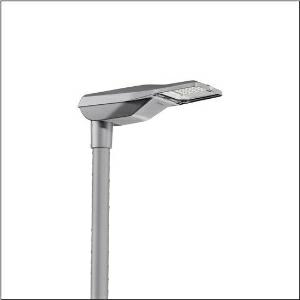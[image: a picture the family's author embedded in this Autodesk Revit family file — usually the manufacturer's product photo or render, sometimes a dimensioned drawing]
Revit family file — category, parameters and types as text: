
# Revit family: streetlight_sl_21_iq_micro___p0_5a_5xe1v31g08db_d973
name_source: partatom
category: Lighting Fixtures
units: mm (PartAtom-declared; Revit-internal decimal feet)

## family parameters
Cut with Voids When Loaded = No
Host = Face
Light Source = No
Part Type = Normal
Room Calculation Point = No
Round Connector Dimension = Use Diameter
Shared = No

## types (1)
- --- (1 x LED, 4660 lm, 36.4 W, 3000K)
    Apparent Load = 36 VA
    CIE Flux Codes = 37 73 96 100 100
    Color Rendering = 70
    Color Temperature = 3000K
    Default Elevation = 1800 mm
    Description = Streetlight SL 21 iQ micro, mast luminaire, primary light control with lens, of PMMA, primary optical cover: cover, of toughened safety glass, transparent, light distribution: P0.5a, light emission: direct distribution, primary light characteristic: asymmetric, installation type: post-top, side-entry, LED, High Power LED, rated luminous flux: 4.660lm, luminous efficacy: 128lm/W, light colour: 730, colour temperature: 3000K, control gear: iQ Street-Remote, control: pre-setting: linear dimming characteristic, Street-Remote, Auto-Match, Temp-Guard, Lumen-Switch, Night-Set, Smart-Wire, Light-Fading, Desk-Remote (wireless, voltage-free reading and setting of iQ features in the workshop via application-optimized NFC function/RFID function), optimised constant luminous flux control (CLO 2.0), mains connection: 220..240V, AC, 50/60Hz, start of lifetime: 36W, end of service life: 38W, reduction: 16W, luminaire housing, of diecast aluminium, powder-coated, Siteco® metallic grey (DB 702S), corrosivity category C5 mid according to DIN EN ISO 12944, please order mast flange separately, inclination adjustable: 0°, 5°, 10°, 15°, sealing non-destructively replaceable, multi-level sealing system, length: 528mm, width: 235mm, height: 110mm, mast flange for spigot size: 42mm (side-entry): 5XC10008XM4, 60/48mm (side-entry/post-top): 5XC10108XM2, 76/60mm (side-entry/post-top): 5XC10108XM1, protection rating (complete): IP66, insulation class (complete): insulation class II (safety insulation), certification: CE, ENEC, ENEC+, VDE, impact resistance: IK10, permissible operating ambient temperature for outdoor applications: -40..+50°C, standard-compliant lighting for roads and squares, packaging unit: 1 piece

Light Distribution: P0.5a
    Height = 110 mm
    Lamp = 1 x LED
    Lamp Light Flux = 4660 lm
    Lamp Power = 36.4 W
    Lamp count = 1
    Length = 528 mm
    Luminous efficacy = 128 lm/W
    Manufacturer = Siteco
    ModVariant = No
    Model = 5XE1V31G08DB
    Number of Poles = 1
    OnlyDefault = Yes
    Power Factor = 1
    Product Name = Streetlight SL 21 iQ micro | P0.5a
    Product group = mast luminaire | pylon top
    ProductGroupID = 6100
    Protection Class = Protection class II
    Protection Degree = IP 66
    RLX_Detail_Level = 1
    RLX_Emergency_Light_Flux = 0 lm
    RLX_Emergency_Type = 0
    RLX_Emergency_Type_DB = No
    RlxData = <blob elided: 98553 chars, md5=35e604e4>
    Socket = socket
    Standby Power = 0 W
    System Light Flux = 4660 lm
    System Power = 36 W
    Type Comments = factory setting: luminous flux: 100 % | dim-lin: 254 | 715 mA
    Type Image = l_1006881.jpg
    URL = http://relux.com
    VarID = @adj_070366
    Voltage = 0 V
    Weight = 0.00 kg
    Width = 235 mm

## geometry (parser evidence)
native form markers: Blend x4, Sweep x10
no freeform markers — native parametric forms only
